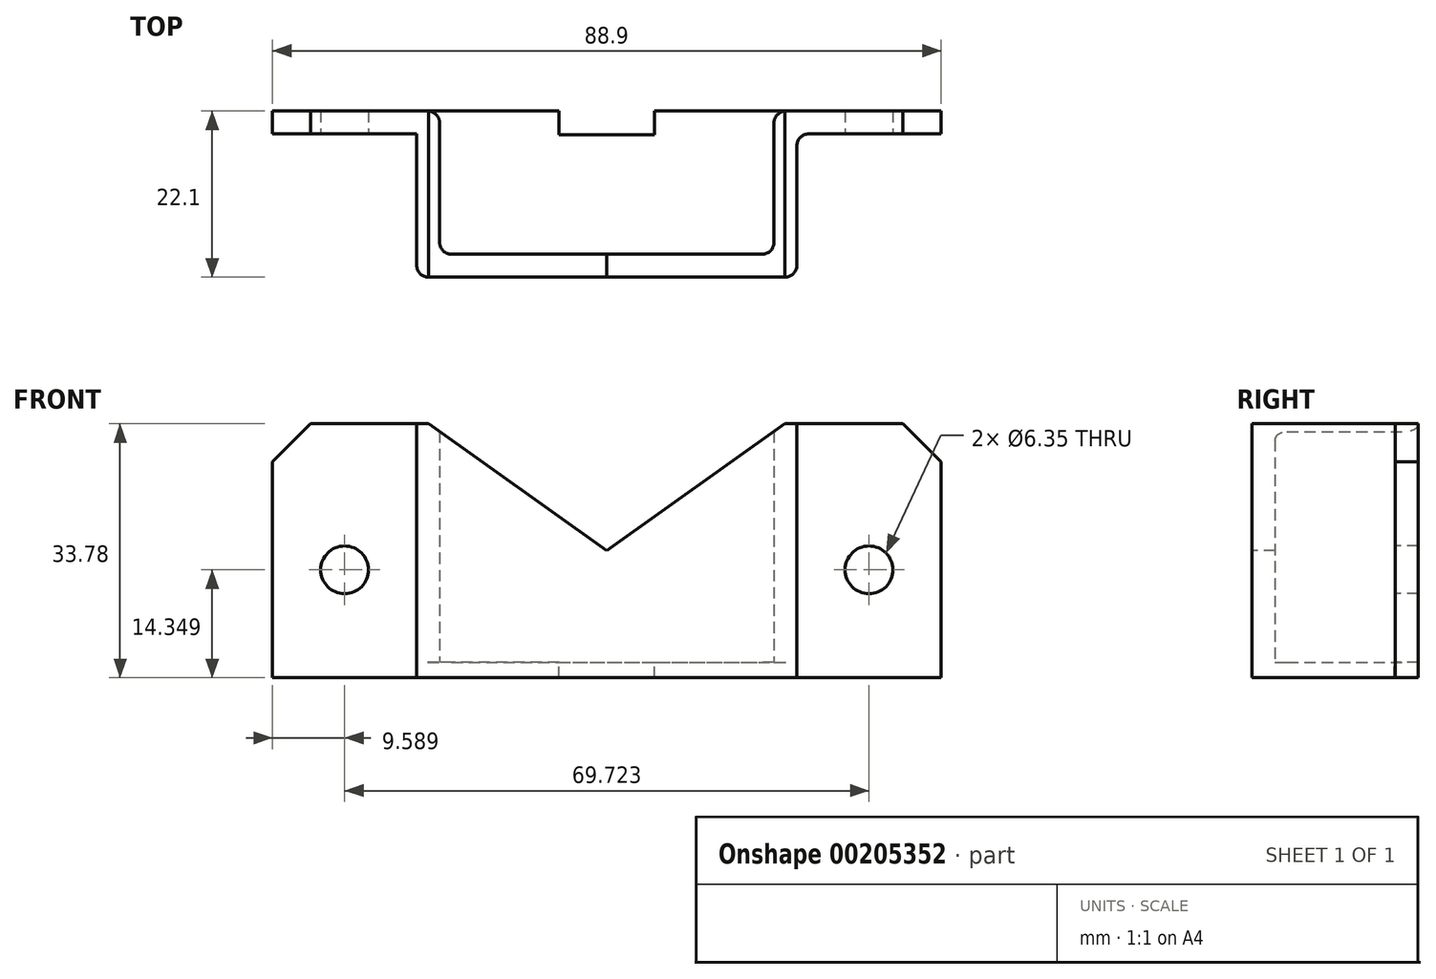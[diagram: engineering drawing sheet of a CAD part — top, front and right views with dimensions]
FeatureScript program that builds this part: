
annotation { "Feature Type Name" : "Feature", "Feature Type Description" : "" }
export const myFeature = defineFeature(function(context is Context, id is Id, definition is map)
    precondition{}
    {
        {
            var Q0;
            Q0=qCreatedBy(makeId("Top.planeOp"),FACE);
            var sketch = newSketch(context, id + "F0", { "sketchPlane" : qUnion([Q0])});
            skLineSegment(sketch, "E0", {"start": v(-25.27, 0) * mm, "end": v(25.27, 0) * mm});
            skLineSegment(sketch, "E1", {"start": v(25.27, 0) * mm, "end": v(25.27, 19.05) * mm});
            skLineSegment(sketch, "E2", {"start": v(25.27, 19.05) * mm, "end": v(44.45, 19.05) * mm});
            skLineSegment(sketch, "E3", {"start": v(-25.27, 0) * mm, "end": v(-25.27, 19.05) * mm});
            skLineSegment(sketch, "E4", {"start": v(-25.27, 19.05) * mm, "end": v(-44.45, 19.05) * mm});
            skLineSegment(sketch, "E5.0", {"start": v(-22.23, 22.1) * mm, "end": v(-44.45, 22.1) * mm});
            skLineSegment(sketch, "E5.1", {"start": v(22.23, 22.1) * mm, "end": v(44.45, 22.1) * mm});
            skLineSegment(sketch, "E5.2", {"start": v(22.23, 3.05) * mm, "end": v(22.23, 22.1) * mm});
            skLineSegment(sketch, "E5.3", {"start": v(-22.23, 3.05) * mm, "end": v(22.23, 3.05) * mm});
            skLineSegment(sketch, "E5.4", {"start": v(-22.23, 3.05) * mm, "end": v(-22.23, 22.1) * mm});
            skLineSegment(sketch, "E6", {"start": v(-44.45, 22.1) * mm, "end": v(-44.45, 19.05) * mm});
            skLineSegment(sketch, "E7", {"start": v(44.45, 22.1) * mm, "end": v(44.45, 19.05) * mm});
            skSolve(sketch);
        }
        {
            var Q0;
            Q0 = qSketchRegion(id + "F0", true);
            extrude(context, id + "F1", {"entities" : qUnion([Q0]), "depth" : 31.75 * mm});
        }
        {
            var Q0;
            Q0=makeQuery(id+"F1.opExtrude","CAP_FACE",FACE,{"disambiguationData":[OSD([sQuery(id+"F0.wireOp",EDGE,"E0"),sQuery(id+"F0.wireOp",EDGE,"E1"),sQuery(id+"F0.wireOp",EDGE,"E2"),sQuery(id+"F0.wireOp",EDGE,"E3"),sQuery(id+"F0.wireOp",EDGE,"E4"),sQuery(id+"F0.wireOp",EDGE,"E5.0"),sQuery(id+"F0.wireOp",EDGE,"E5.1"),sQuery(id+"F0.wireOp",EDGE,"E5.2"),sQuery(id+"F0.wireOp",EDGE,"E5.3"),sQuery(id+"F0.wireOp",EDGE,"E5.4"),sQuery(id+"F0.wireOp",EDGE,"E6"),sQuery(id+"F0.wireOp",EDGE,"E7")])],"isStart":true});
            var sketch = newSketch(context, id + "F2", { "sketchPlane" : qUnion([Q0])});
            skLineSegment(sketch, "E8.bottom", {"start": v(-25.27, 0) * mm, "end": v(25.27, 0) * mm});
            skLineSegment(sketch, "E8.top", {"start": v(-25.27, -22.1) * mm, "end": v(-6.35, -22.1) * mm});
            skLineSegment(sketch, "E8.left", {"start": v(-25.27, 0) * mm, "end": v(-25.27, -19.05) * mm});
            skLineSegment(sketch, "E8.right", {"start": v(25.27, 0) * mm, "end": v(25.27, -19.05) * mm});
            skLineSegment(sketch, "E9", {"start": v(-25.27, -19.05) * mm, "end": v(-44.45, -19.05) * mm});
            skLineSegment(sketch, "E10", {"start": v(-44.45, -19.05) * mm, "end": v(-44.45, -22.1) * mm});
            skLineSegment(sketch, "E11", {"start": v(-44.45, -22.1) * mm, "end": v(-25.27, -22.1) * mm});
            skLineSegment(sketch, "E12", {"start": v(25.27, -19.05) * mm, "end": v(44.45, -19.05) * mm});
            skLineSegment(sketch, "E13", {"start": v(44.45, -19.05) * mm, "end": v(44.45, -22.1) * mm});
            skLineSegment(sketch, "E14", {"start": v(44.45, -22.1) * mm, "end": v(25.27, -22.1) * mm});
            skLineSegment(sketch, "E15.trimOffspring", {"start": v(6.35, -22.1) * mm, "end": v(25.27, -22.1) * mm});
            skLineSegment(sketch, "E16", {"start": v(-6.35, -22.1) * mm, "end": v(-6.35, -18.92) * mm});
            skLineSegment(sketch, "E17", {"start": v(-6.35, -18.92) * mm, "end": v(6.35, -18.92) * mm});
            skLineSegment(sketch, "E18", {"start": v(6.35, -18.92) * mm, "end": v(6.35, -22.1) * mm});
            skSolve(sketch);
        }
        {
            var Q0;
            Q0 = qSketchRegion(id + "F2", true);
            extrude(context, id + "F3", {"entities" : qUnion([Q0]), "operationType" : NewBodyOperationType.ADD, "depth" : 2.03 * mm});
        }
        {
            var Q0;
            Q0=makeQuery(id+"F1.opExtrude","CAP_EDGE",EDGE,{"disambiguationData":[OSD([sQuery(id+"F0.wireOp",EDGE,"E7")])],"isStart":false});
            var Q1;
            Q1=makeQuery(id+"F1.opExtrude","CAP_EDGE",EDGE,{"disambiguationData":[OSD([sQuery(id+"F0.wireOp",EDGE,"E6")])],"isStart":false});
            chamfer(context, id + "F4", {"entities" : qUnion([Q0, Q1]), "width" : 5.08 * mm, "tangentPropagation" : true});
        }
        {
            var Q0;
            Q0=makeQuery(id+"F3.boolean.opBoolean","MERGE",FACE,{"derivedFrom":[makeQuery(id+"F1.opExtrude","SWEPT_FACE",FACE,{"disambiguationData":[OSD([sQuery(id+"F0.wireOp",EDGE,"E4")])]}),makeQuery(id+"F3.opExtrude","SWEPT_FACE",FACE,{"disambiguationData":[OSD([sQuery(id+"F2.wireOp",EDGE,"E9")])]})]});
            var sketch = newSketch(context, id + "F5", { "sketchPlane" : qUnion([Q0])});
            skPoint(sketch, "E19.centerSnap0", {"position": v(-44.45, 12.32) * mm});
            skLineSegment(sketch, "E20", {"start": v(-44.45, 26.67) * mm, "end": v(-25.27, 26.67) * mm, "construction": true});
            skCircle(sketch, "E21", {"center": v(-34.86, 12.32) * mm, "radius": 3.18 * mm});
            skPoint(sketch, "E21.centerSnap0", {"position": v(-34.86, 26.67) * mm});
            skCircle(sketch, "E22.MirrorC", {"center": v(34.86, 12.32) * mm, "radius": 3.18 * mm});
            skSolve(sketch);
        }
        {
            var Q0;
            Q0 = qSketchRegion(id + "F5", true);
            extrude(context, id + "F6", {"entities" : qUnion([Q0]), "operationType" : NewBodyOperationType.REMOVE, "endBound" : BoundingType.UP_TO_NEXT, "oppositeDirection" : true, "depth" : 25.4 * mm});
        }
        {
            var Q0;
            Q0=makeQuery(id+"F3.boolean.opBoolean","MERGE",EDGE,{"derivedFrom":[makeQuery(id+"F1.opExtrude","SWEPT_EDGE",EDGE,{"disambiguationData":[OSD([sQuery(id+"F0.wireOp",EDGE,"E0"),sQuery(id+"F0.wireOp",EDGE,"E1")])]}),makeQuery(id+"F3.opExtrude","SWEPT_EDGE",EDGE,{"disambiguationData":[OSD([sQuery(id+"F2.wireOp",EDGE,"E8.bottom"),sQuery(id+"F2.wireOp",EDGE,"E8.right")])]})]});
            var Q1;
            Q1=makeQuery(id+"F3.boolean.opBoolean","MERGE",EDGE,{"derivedFrom":[makeQuery(id+"F1.opExtrude","SWEPT_EDGE",EDGE,{"disambiguationData":[OSD([sQuery(id+"F0.wireOp",EDGE,"E0"),sQuery(id+"F0.wireOp",EDGE,"E3")])]}),makeQuery(id+"F3.opExtrude","SWEPT_EDGE",EDGE,{"disambiguationData":[OSD([sQuery(id+"F2.wireOp",EDGE,"E8.bottom"),sQuery(id+"F2.wireOp",EDGE,"E8.left")])]})]});
            var Q2;
            Q2=makeQuery(id+"F3.boolean.opBoolean","MERGE",EDGE,{"derivedFrom":[makeQuery(id+"F1.opExtrude","SWEPT_EDGE",EDGE,{"disambiguationData":[OSD([sQuery(id+"F0.wireOp",EDGE,"E1"),sQuery(id+"F0.wireOp",EDGE,"E2")])]}),makeQuery(id+"F3.opExtrude","SWEPT_EDGE",EDGE,{"disambiguationData":[OSD([sQuery(id+"F2.wireOp",EDGE,"E8.right"),sQuery(id+"F2.wireOp",EDGE,"E12")])]})]});
            var Q3;
            Q3=makeQuery(id+"F1.opExtrude","SWEPT_EDGE",EDGE,{"disambiguationData":[OSD([sQuery(id+"F0.wireOp",EDGE,"E5.2"),sQuery(id+"F0.wireOp",EDGE,"E5.3")])]});
            var Q4;
            Q4=makeQuery(id+"F1.opExtrude","SWEPT_EDGE",EDGE,{"disambiguationData":[OSD([sQuery(id+"F0.wireOp",EDGE,"E5.1"),sQuery(id+"F0.wireOp",EDGE,"E5.2")])]});
            var Q5;
            Q5=makeQuery(id+"F1.opExtrude","SWEPT_EDGE",EDGE,{"disambiguationData":[OSD([sQuery(id+"F0.wireOp",EDGE,"E5.3"),sQuery(id+"F0.wireOp",EDGE,"E5.4")])]});
            var Q6;
            Q6=makeQuery(id+"F1.opExtrude","SWEPT_EDGE",EDGE,{"disambiguationData":[OSD([sQuery(id+"F0.wireOp",EDGE,"E5.0"),sQuery(id+"F0.wireOp",EDGE,"E5.4")])]});
            fillet(context, id + "F7", {"entities" : qUnion([Q0, Q1, Q2, Q3, Q4, Q5, Q6]), "radius" : 1.59 * mm, "tangentPropagation" : true, "allowEdgeOverflow" : false});
        }
        {
            var Q0;
            Q0=makeQuery(id+"F3.boolean.opBoolean","MERGE",FACE,{"derivedFrom":[makeQuery(id+"F1.opExtrude","SWEPT_FACE",FACE,{"disambiguationData":[OSD([sQuery(id+"F0.wireOp",EDGE,"E0")])]}),makeQuery(id+"F3.opExtrude","SWEPT_FACE",FACE,{"disambiguationData":[OSD([sQuery(id+"F2.wireOp",EDGE,"E8.bottom")])]})]});
            var sketch = newSketch(context, id + "F8", { "sketchPlane" : qUnion([Q0])});
            skLineSegment(sketch, "E23", {"start": v(-23.69, 31.75) * mm, "end": v(0, 14.86) * mm});
            skPoint(sketch, "E23.endSnap0", {"position": v(0, 31.75) * mm});
            skPoint(sketch, "E23.endSnap1", {"position": v(-23.69, 14.86) * mm});
            skLineSegment(sketch, "E24", {"start": v(0, 14.86) * mm, "end": v(23.69, 31.75) * mm});
            skLineSegment(sketch, "E25", {"start": v(23.69, 31.75) * mm, "end": v(-23.69, 31.75) * mm});
            skSolve(sketch);
        }
        {
            var Q0;
            Q0 = qSketchRegion(id + "F8", true);
            extrude(context, id + "F9", {"entities" : qUnion([Q0]), "operationType" : NewBodyOperationType.REMOVE, "endBound" : BoundingType.UP_TO_NEXT, "oppositeDirection" : true, "depth" : 25.4 * mm});
        }
    });
